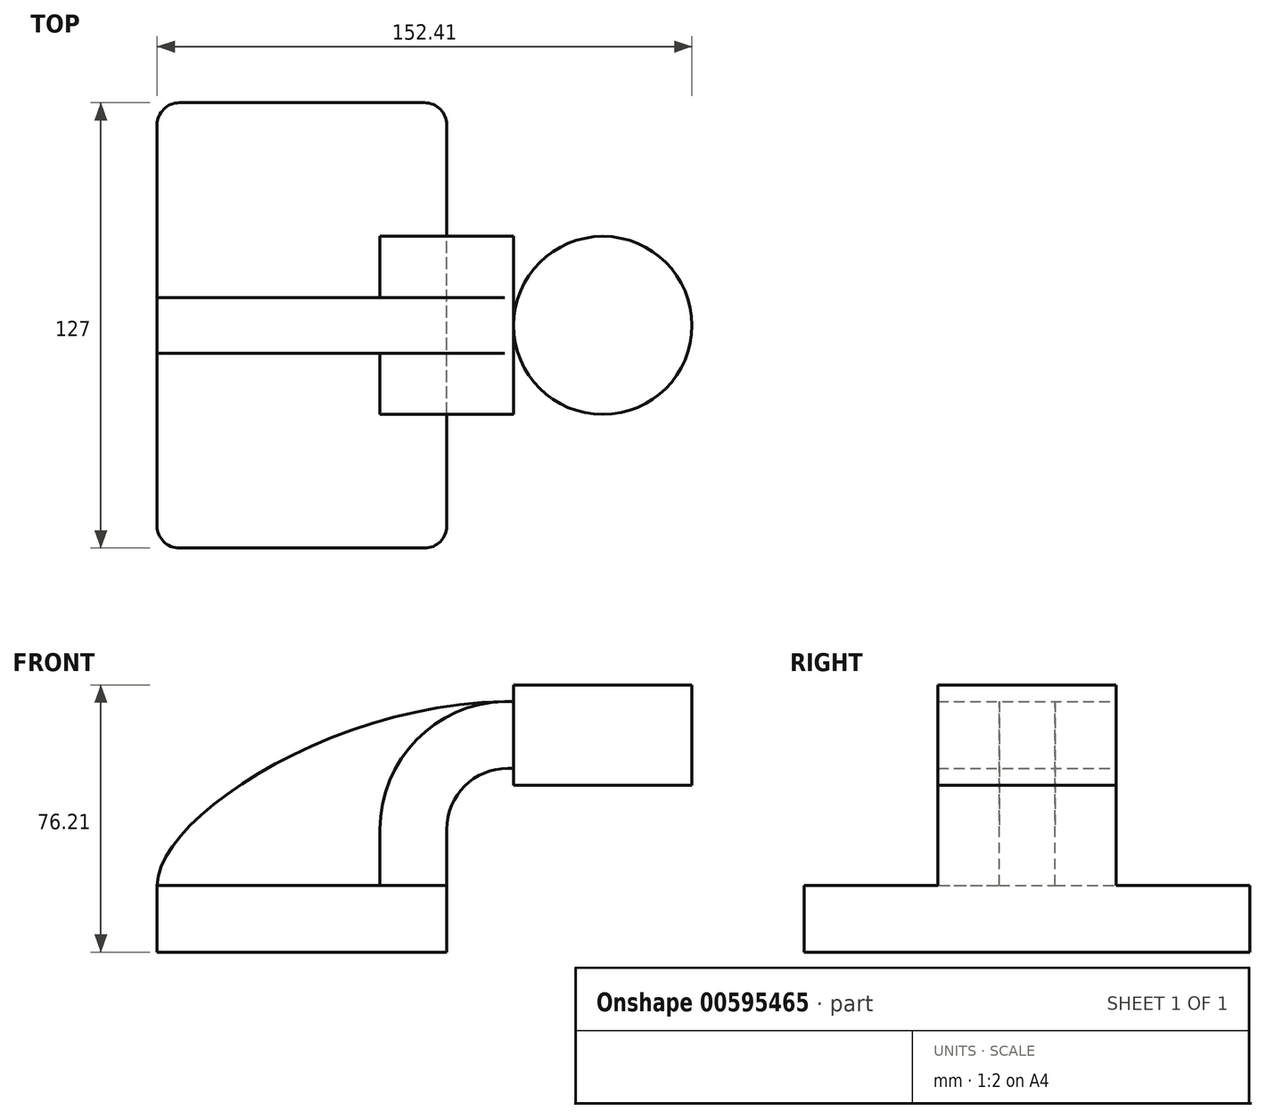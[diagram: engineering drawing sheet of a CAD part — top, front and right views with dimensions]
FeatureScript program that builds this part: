
annotation { "Feature Type Name" : "Feature", "Feature Type Description" : "" }
export const myFeature = defineFeature(function(context is Context, id is Id, definition is map)
    precondition{}
    {
        {
            var Q0;
            Q0=qCreatedBy(makeId("Front.planeOp"),FACE);
            var sketch = newSketch(context, id + "F0", { "sketchPlane" : qUnion([Q0])});
            skLineSegment(sketch, "E0.bottom", {"start": v(-41.28, -9.53) * mm, "end": v(41.28, -9.53) * mm});
            skLineSegment(sketch, "E0.top", {"start": v(-41.28, 9.53) * mm, "end": v(41.28, 9.53) * mm});
            skLineSegment(sketch, "E0.left", {"start": v(-41.28, -9.53) * mm, "end": v(-41.28, 9.53) * mm});
            skLineSegment(sketch, "E0.right", {"start": v(41.28, -9.53) * mm, "end": v(41.28, 9.53) * mm});
            skPoint(sketch, "E0.middle", {"position": v(0, 0) * mm});
            skLineSegment(sketch, "E1.bottom", {"start": v(60.32, 38.1) * mm, "end": v(111.12, 38.1) * mm});
            skLineSegment(sketch, "E1.top", {"start": v(60.32, 66.67) * mm, "end": v(111.12, 66.67) * mm});
            skLineSegment(sketch, "E1.left", {"start": v(60.32, 38.1) * mm, "end": v(60.32, 66.67) * mm});
            skLineSegment(sketch, "E1.right", {"start": v(111.12, 38.1) * mm, "end": v(111.12, 66.67) * mm});
            skPoint(sketch, "E1.middle", {"position": v(85.72, 52.39) * mm});
            skLineSegment(sketch, "E2", {"start": v(41.28, 9.53) * mm, "end": v(41.28, 25.53) * mm});
            skLineSegment(sketch, "E3", {"start": v(85.72, 42.88) * mm, "end": v(58.62, 42.88) * mm});
            skArc(sketch, "E4", {"start": v(41.27, 25.53) * mm, "mid": v(46.36, 37.8) * mm, "end": v(58.62, 42.88) * mm});
            skLineSegment(sketch, "E5.0", {"start": v(85.72, 61.93) * mm, "end": v(58.62, 61.93) * mm});
            skArc(sketch, "E5.1", {"start": v(22.22, 25.53) * mm, "mid": v(32.89, 51.26) * mm, "end": v(58.62, 61.93) * mm});
            skLineSegment(sketch, "E5.2", {"start": v(22.22, 9.53) * mm, "end": v(22.22, 25.53) * mm});
            skLineSegment(sketch, "E6", {"start": v(85.72, 38.1) * mm, "end": v(85.72, 66.67) * mm});
            skFitSpline(sketch, "E7", {"points": [v(-41.28, 9.53) * mm, v(58.62, 61.93) * mm], "startDerivative": vector(1, 58.73) * mm, "endDerivative": vector(148.54, 1.2) * mm});
            skSolve(sketch);
        }
        {
            var Q0;
            Q0=makeQuery(id+"F0.imprint","IMPRINT",FACE,{"disambiguationData":[TD([[makeQuery(id+"F0.imprint","IMPRINT",EDGE,{"derivedFrom":sQuery(id+"F0.wireOp",EDGE,"E0.bottom")}),1.0]])]});
            extrude(context, id + "F1", {"entities" : qUnion([Q0]), "endBound" : BoundingType.SYMMETRIC, "depth" : 127 * mm, "offsetDistance" : 25.4 * mm});
        }
        {
            var Q0;
            {var subQ0=sQuery(id+"F0.wireOp",EDGE,"E2");Q0=makeQuery(id+"F0.imprint","IMPRINT",FACE,{"disambiguationData":[TD([[makeQuery(id+"F0.imprint","IMPRINT",EDGE,{"derivedFrom":subQ0}),1.0]])]});}
            extrude(context, id + "F2", {"entities" : qUnion([Q0]), "operationType" : NewBodyOperationType.ADD, "endBound" : BoundingType.SYMMETRIC, "depth" : 50.8 * mm, "offsetDistance" : 25.4 * mm});
        }
        {
            var Q0;
            {var subQ3=sQuery(id+"F0.wireOp",EDGE,"E5.2");Q0=makeQuery(id+"F0.imprint","IMPRINT",FACE,{"disambiguationData":[TD([[makeQuery(id+"F0.imprint","IMPRINT",EDGE,{"derivedFrom":subQ3}),1.0]])]});}
            extrude(context, id + "F3", {"entities" : qUnion([Q0]), "operationType" : NewBodyOperationType.ADD, "endBound" : BoundingType.SYMMETRIC, "depth" : 15.88 * mm, "offsetDistance" : 25.4 * mm});
        }
        {
            var Q0;
            {var subQ4=sQuery(id+"F0.wireOp",EDGE,"E1.right");Q0=makeQuery(id+"F0.imprint","IMPRINT",FACE,{"disambiguationData":[TD([[makeQuery(id+"F0.imprint","IMPRINT",EDGE,{"derivedFrom":subQ4}),1.0]])]});}
            var Q1;
            Q1=sQuery(id+"F0.wireOp",EDGE,"E6");
            revolve(context, id + "F4", {"operationType" : NewBodyOperationType.ADD, "entities" : qUnion([Q0]), "axis" : qUnion([Q1]), "revolveType" : RevolveType.FULL});
        }
        {
            var Q0;
            Q0=makeQuery(id+"F1.opExtrude","CAP_EDGE",EDGE,{"disambiguationData":[OSD([sQuery(id+"F0.wireOp",EDGE,"E0.right")])],"isStart":false});
            var Q1;
            Q1=makeQuery(id+"F1.opExtrude","CAP_EDGE",EDGE,{"disambiguationData":[OSD([sQuery(id+"F0.wireOp",EDGE,"E0.left")])],"isStart":false});
            var Q2;
            Q2=makeQuery(id+"F1.opExtrude","CAP_EDGE",EDGE,{"disambiguationData":[OSD([sQuery(id+"F0.wireOp",EDGE,"E0.right")])],"isStart":true});
            var Q3;
            Q3=makeQuery(id+"F1.opExtrude","CAP_EDGE",EDGE,{"disambiguationData":[OSD([sQuery(id+"F0.wireOp",EDGE,"E0.left")])],"isStart":true});
            fillet(context, id + "F5", {"entities" : qUnion([Q0, Q1, Q2, Q3]), "radius" : 6.35 * mm, "tangentPropagation" : true, "allowEdgeOverflow" : false});
        }
    });
